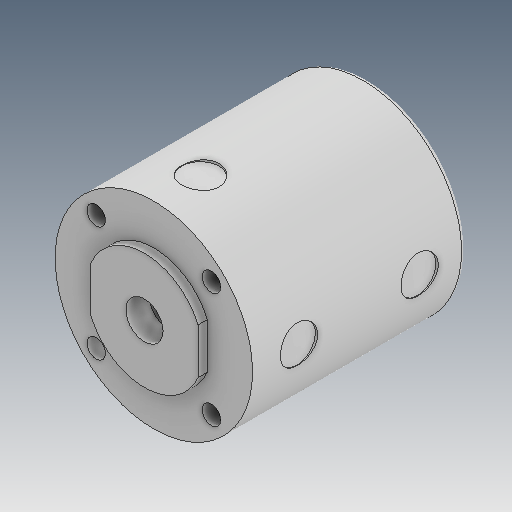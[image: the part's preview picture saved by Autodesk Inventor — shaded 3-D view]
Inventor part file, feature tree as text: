
AUTODESK INVENTOR PART (.ipt)
format: ipt  version: 2020 (Build 240168000, 168)  size: 208,384 bytes
history: native  units: mm
features: extrude x6, sketch x6, other x3, pattern_circular x1, fillet x1, projected_geometry x1
ambient origin geometry x8: Origin, YZ Plane, XZ Plane, XY Plane, X Axis, Y Axis, Z Axis, Center Point
bodies: Body1 (feature_tree)
feature tree (18):
  other  "솔리드1"
  extrude  "돌출1"  Depth=42.4mm
  extrude  "돌출2"  Depth=45.9mm TaperAngle=0.0deg
  extrude  "돌출3"  Depth=40.0mm TaperAngle=360.0deg
  extrude  "돌출4"  Depth=6.0mm TaperAngle=0.0deg
  other  "작업 평면1"
  extrude  "돌출5"  Depth=40.0mm TaperAngle=360.0deg
  other  "작업 평면5"
  extrude  "돌출7"  Depth=2.0mm TaperAngle=0.0deg
  pattern_circular  "원형 패턴2"  [2 undecoded]
  fillet  "모깎기1"  Radius=5.0mm
  sketch  "스케치1"
  sketch  "스케치2"
  sketch  "스케치3"
  sketch  "스케치4"
  sketch  "스케치5"
  projected_geometry  "투영된 루프1"
  sketch  "스케치7"
note: 2 required parameter values undecoded (feature->parameter linkage not recoverable at this tier; creation-order binding heuristic only, values carry confidence <= 0.55)
